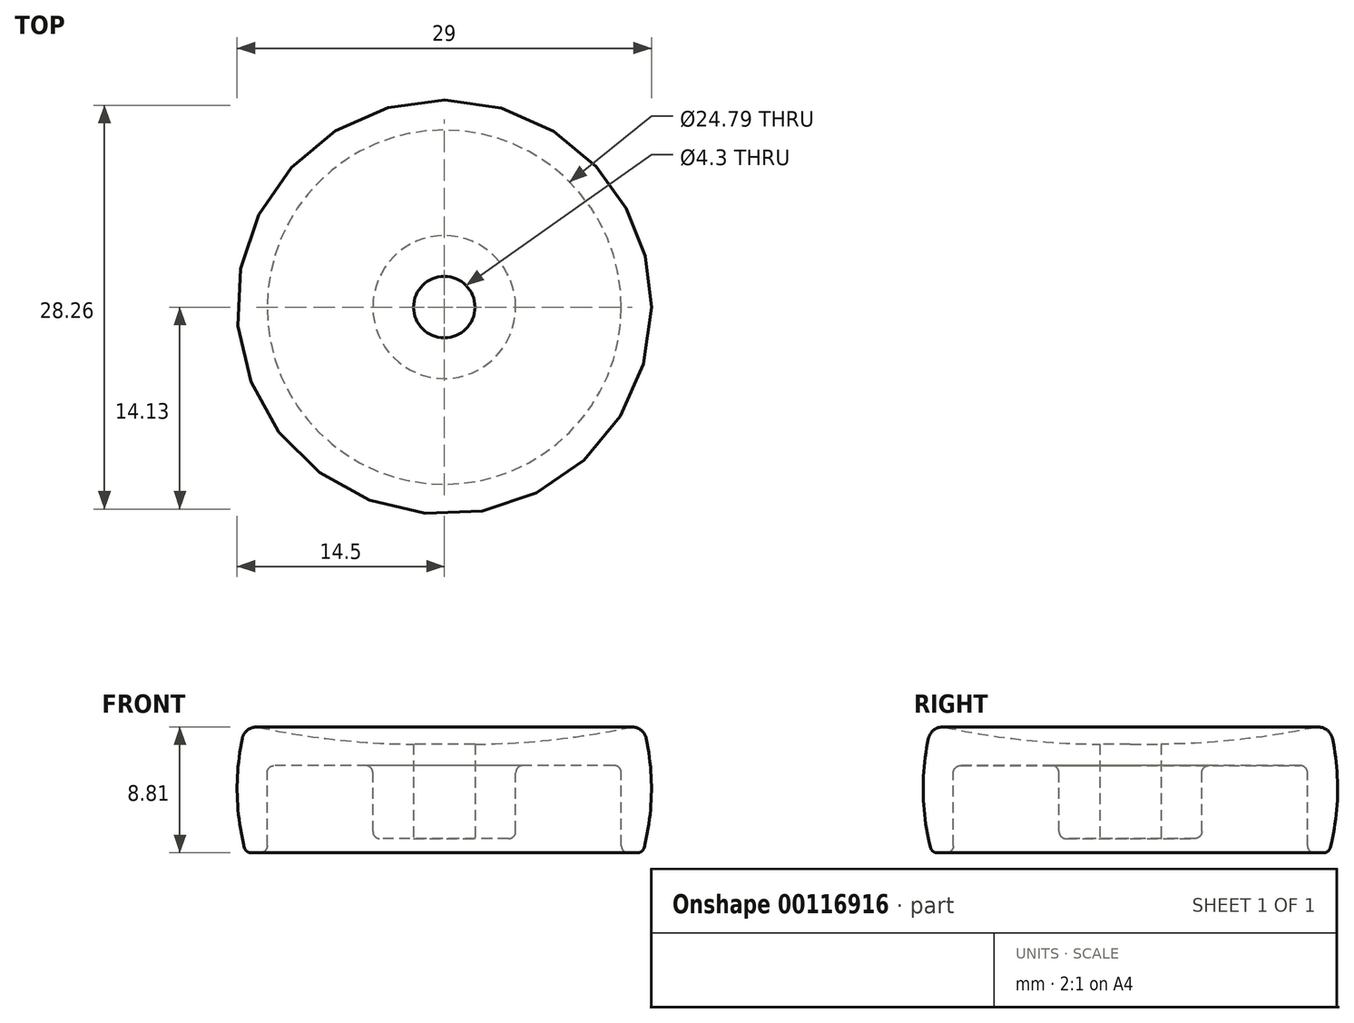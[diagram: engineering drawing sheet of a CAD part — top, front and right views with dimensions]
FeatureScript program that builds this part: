
annotation { "Feature Type Name" : "Feature", "Feature Type Description" : "" }
export const myFeature = defineFeature(function(context is Context, id is Id, definition is map)
    precondition{}
    {
        {
            var Q0;
            Q0=qCreatedBy(makeId("Front.planeOp"),FACE);
            var sketch = newSketch(context, id + "F0", { "sketchPlane" : qUnion([Q0])});
            skLineSegment(sketch, "E0", {"start": v(0, 13.56) * mm, "end": v(0, -5.85) * mm, "construction": true});
            skLineSegment(sketch, "E1", {"start": v(5, 5.6) * mm, "end": v(5, 1.5) * mm});
            skArc(sketch, "E2", {"start": v(14, 0.38) * mm, "mid": v(14.5, 4.19) * mm, "end": v(14.13, 8.02) * mm});
            skArc(sketch, "E3", {"start": v(0, 7.64) * mm, "mid": v(6.5, 7.81) * mm, "end": v(12.94, 8.79) * mm});
            skLineSegment(sketch, "E4", {"start": v(13.5, 0) * mm, "end": v(12.9, 0) * mm});
            skLineSegment(sketch, "E5", {"start": v(12.4, 0.5) * mm, "end": v(12.4, 5.6) * mm});
            skLineSegment(sketch, "E6", {"start": v(11.9, 6.1) * mm, "end": v(5.5, 6.1) * mm});
            skPoint(sketch, "E7.visualSharp", {"position": v(13.9, 9) * mm});
            skArc(sketch, "E7.filletArc", {"start": v(14.13, 8.02) * mm, "mid": v(13.7, 8.65) * mm, "end": v(12.94, 8.79) * mm});
            skPoint(sketch, "E8.visualSharp", {"position": v(13.9, 0) * mm});
            skArc(sketch, "E8.filletArc", {"start": v(13.5, 0) * mm, "mid": v(13.82, 0.1) * mm, "end": v(14, 0.38) * mm});
            skPoint(sketch, "E9.visualSharp", {"position": v(12.4, 0) * mm});
            skArc(sketch, "E9.filletArc", {"start": v(12.4, 0.5) * mm, "mid": v(12.54, 0.15) * mm, "end": v(12.9, 0) * mm});
            skPoint(sketch, "E10.visualSharp", {"position": v(12.4, 6.1) * mm});
            skArc(sketch, "E10.filletArc", {"start": v(12.4, 5.6) * mm, "mid": v(12.25, 5.96) * mm, "end": v(11.9, 6.1) * mm});
            skPoint(sketch, "E11.visualSharp", {"position": v(5, 6.1) * mm});
            skArc(sketch, "E11.filletArc", {"start": v(5.5, 6.1) * mm, "mid": v(5.15, 5.96) * mm, "end": v(5, 5.6) * mm});
            skLineSegment(sketch, "E12", {"start": v(0, 1) * mm, "end": v(4.5, 1) * mm});
            skPoint(sketch, "E13.visualSharp", {"position": v(5, 1) * mm});
            skArc(sketch, "E13.filletArc", {"start": v(4.5, 1) * mm, "mid": v(4.85, 1.15) * mm, "end": v(5, 1.5) * mm});
            skLineSegment(sketch, "E14", {"start": v(0, 7.64) * mm, "end": v(0, 1) * mm});
            skSolve(sketch);
        }
        {
            var Q0;
            Q0 = qSketchRegion(id + "F0", true);
            var Q1;
            Q1=sQuery(id+"F0.wireOp",EDGE,"E0");
            revolve(context, id + "F1", {"entities" : qUnion([Q0]), "axis" : qUnion([Q1]), "revolveType" : RevolveType.FULL});
        }
        {
            var Q0;
            Q0=makeQuery(id+"F1.opRevolve","SWEPT_FACE",FACE,{"disambiguationData":[OSD([sQuery(id+"F0.wireOp",EDGE,"E12")])]});
            var sketch = newSketch(context, id + "F2", { "sketchPlane" : qUnion([Q0])});
            skSolve(sketch);
        }
        {
            var Q0;
            Q0=makeQuery(id+"F2.imprint","IMPRINT",FACE,{"disambiguationData":[TD([[makeQuery(id+"F2.imprint","IMPRINT",EDGE,{"derivedFrom":makeQuery(id+"F1.opRevolve","SWEPT_EDGE",EDGE,{"disambiguationData":[OSD([sQuery(id+"F0.wireOp",EDGE,"E12"),sQuery(id+"F0.wireOp",EDGE,"E13.filletArc")])]})}),-1.0]])]});
            var sketch = newSketch(context, id + "F3", { "sketchPlane" : qUnion([Q0])});
            skLineSegment(sketch, "E15", {"start": v(0, 3.84) * mm, "end": v(0, -3.74) * mm, "construction": true});
            skLineSegment(sketch, "E16", {"start": v(-3.48, 0) * mm, "end": v(3.16, 0) * mm, "construction": true});
            skPoint(sketch, "E17", {"position": v(0, 0) * mm});
            skPoint(sketch, "E18", {"position": v(0, 0.03) * mm});
            skSolve(sketch);
        }
        {
            var Q0;
            Q0=sQuery(id+"F3.wireOp",VERTEX,"E17");
            var Q1;
            Q1=makeQuery(id+"F1.opRevolve","SWEPT_BODY",BODY,{"disambiguationData":[OSD([sQuery(id+"F0.wireOp",EDGE,"E1"),sQuery(id+"F0.wireOp",EDGE,"E2"),sQuery(id+"F0.wireOp",EDGE,"E3"),sQuery(id+"F0.wireOp",EDGE,"E4"),sQuery(id+"F0.wireOp",EDGE,"E5"),sQuery(id+"F0.wireOp",EDGE,"E6"),sQuery(id+"F0.wireOp",EDGE,"E7.filletArc"),sQuery(id+"F0.wireOp",EDGE,"E8.filletArc"),sQuery(id+"F0.wireOp",EDGE,"E9.filletArc"),sQuery(id+"F0.wireOp",EDGE,"E10.filletArc"),sQuery(id+"F0.wireOp",EDGE,"E11.filletArc"),sQuery(id+"F0.wireOp",EDGE,"E12"),sQuery(id+"F0.wireOp",EDGE,"E13.filletArc"),sQuery(id+"F0.wireOp",EDGE,"E14")])]});
            hole(context, id + "F4", {"style" : HoleStyle.SIMPLE, "endStyle" : HoleEndStyle.THROUGH, "holeDiameter" : 4.3 * mm, "locations" : qUnion([Q0]), "scope" : qUnion([Q1]), "tappedDepth" : 12 * mm, "tapClearance" : 3});
        }
    });
